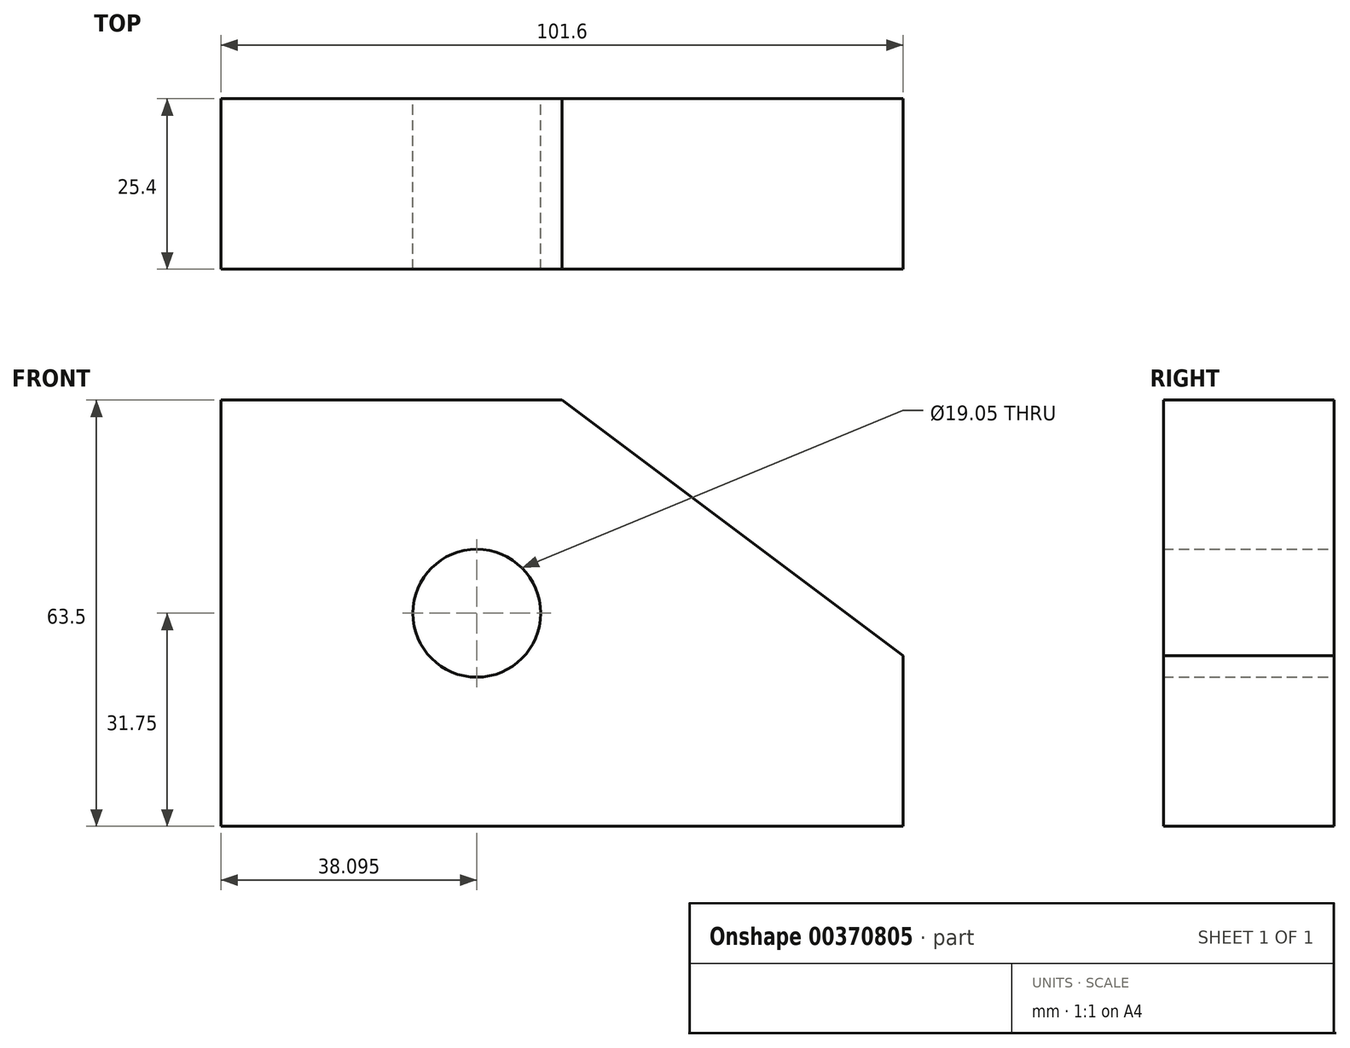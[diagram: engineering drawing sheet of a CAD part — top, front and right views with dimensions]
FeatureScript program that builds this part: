
annotation { "Feature Type Name" : "Feature", "Feature Type Description" : "" }
export const myFeature = defineFeature(function(context is Context, id is Id, definition is map)
    precondition{}
    {
        {
            var Q0;
            Q0=qCreatedBy(makeId("Front.planeOp"),FACE);
            var sketch = newSketch(context, id + "F0", { "sketchPlane" : qUnion([Q0])});
            skLineSegment(sketch, "E0", {"start": v(-39.24, 31.75) * mm, "end": v(-39.24, -31.75) * mm});
            skLineSegment(sketch, "E1", {"start": v(-39.24, -31.75) * mm, "end": v(62.36, -31.75) * mm});
            skLineSegment(sketch, "E2", {"start": v(62.36, -31.75) * mm, "end": v(62.36, -6.35) * mm});
            skLineSegment(sketch, "E3", {"start": v(62.36, -6.35) * mm, "end": v(11.56, 31.75) * mm});
            skLineSegment(sketch, "E4", {"start": v(11.56, 31.75) * mm, "end": v(-39.24, 31.75) * mm});
            skCircle(sketch, "E5", {"center": v(-1.14, 0) * mm, "radius": 9.53 * mm});
            skSolve(sketch);
        }
        {
            var Q0;
            Q0=makeQuery(id+"F0.imprint","IMPRINT",FACE,{"disambiguationData":[TD([[makeQuery(id+"F0.imprint","IMPRINT",EDGE,{"derivedFrom":sQuery(id+"F0.wireOp",EDGE,"E0")}),1.0]])]});
            extrude(context, id + "F1", {"entities" : qUnion([Q0]), "depth" : 25.4 * mm});
        }
    });
